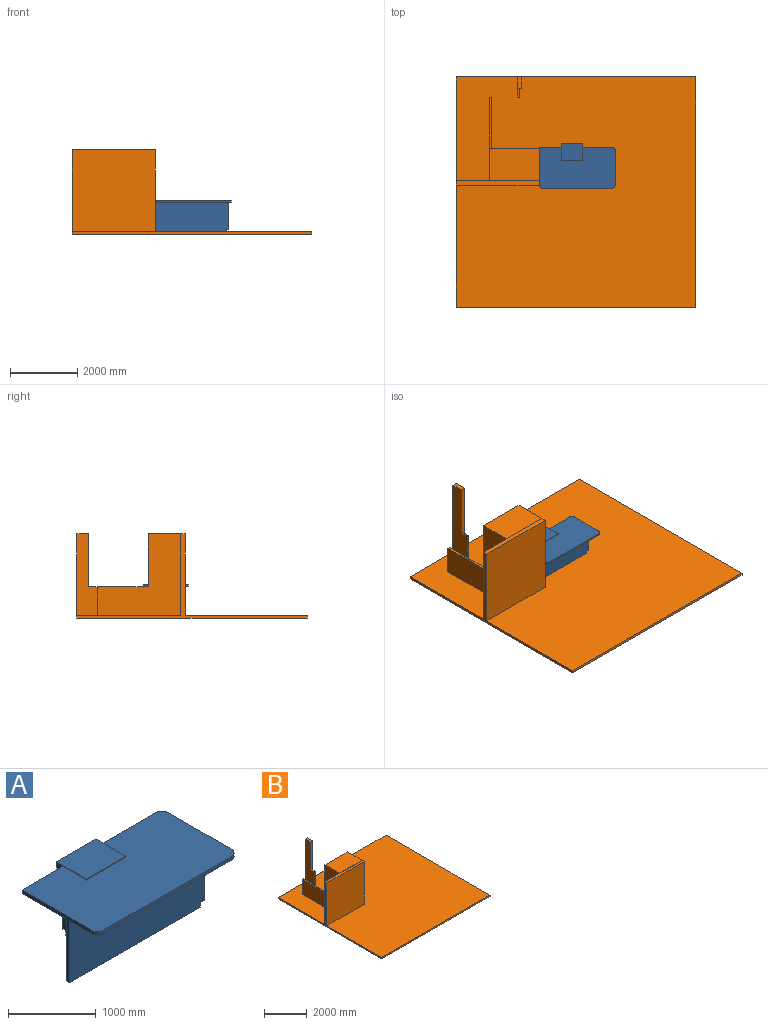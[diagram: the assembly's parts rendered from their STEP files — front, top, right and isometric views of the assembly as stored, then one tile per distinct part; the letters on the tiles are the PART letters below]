
ASSEMBLY  parts=2 mates=2
PART A: 30 faces, bbox 2260.6x1320.8x927.1 mm
  f0: plane 800.1x736.6mm, normal (1,0,0), area 589353.7mm2, adj f3,f5,f7,f28
  f1: plane 1117.6x914.4mm, normal (-1,0,0), area 100645mm2, adj f2,f7,f8,f11,f12,f22,f28,f29
  f2: plane 2114.55x692.15mm, normal (0,0,-1), area 1056328.5mm2, adj f1,f4,f21,f22,f23,f28
  f3: plane 1549.4x736.6mm, normal (0,0,-1), area 117217.5mm2, adj f0,f4,f5,f21,f23,f28
  f4: plane 692.15x63.5mm, normal (1,0,0), area 43951.5mm2, adj f2,f3,f23,f28
  f5: plane 1549.4x800.1mm, normal (0,1,0), area 536289.2mm2, adj f0,f3,f7,f12,f15,f17,f20,f21
  f6: plane 863.6x50.8mm, normal (0,1,0), area 43870.9mm2, adj f7,f11,f14,f17
  f7: plane 2260.6x1219.2mm, normal (0,0,-1), area 1561738.2mm2, adj f0,f1,f5,f6,f9,f10,f13,f14
  f8: plane 660.4x50.8mm, normal (0,1,0), area 33548.3mm2, adj f1,f11,f12,f15
  f9: plane 2057.4x50.8mm, normal (0,-1,0), area 104515.9mm2, adj f7,f11,f13,f29
  f10: plane 1016x50.8mm, normal (1,0,0), area 51612.8mm2, adj f7,f11,f13,f14
  f11: plane 2260.6x1219.2mm, normal (0,0,1), area 2507542.8mm2, adj f1,f6,f8,f9,f10,f13,f14,f15
  f12: plane 711.2x660.4mm, normal (0,0,-1), area 452257.2mm2, adj f1,f5,f8,f15,f21,f22
  f13: cylinder r=101.6mm len=101.6mm, axis (0,0,1), area 8107.3mm2, adj f7,f9,f10,f11
  f14: cylinder r=101.6mm len=101.6mm, axis (0,0,-1), area 8107.3mm2, adj f6,f7,f10,f11
  f15: plane 482.6x171.45mm, normal (-1,0,0), area 25000mm2, adj f5,f8,f11,f12,f16,f18,f19,f20
  f16: plane 635x12.7mm, normal (0,-1,0), area 8064.5mm2, adj f11,f15,f17,f19
  f17: plane 482.6x171.45mm, normal (1,0,0), area 25000mm2, adj f5,f6,f7,f11,f16,f18,f19,f20
  f18: plane 635x171.45mm, normal (0,1,0), area 108870.8mm2, adj f15,f17,f19,f20
  f19: plane 635x482.6mm, normal (0,0,1), area 306451mm2, adj f15,f16,f17,f18
  f20: plane 635x127mm, normal (0,0,-1), area 80645mm2, adj f5,f15,f17,f18
  f21: plane 863.6x685.8mm, normal (-1,0,0), area 589434.3mm2, adj f2,f3,f5,f12,f22,f23
  f22: plane 863.6x635mm, normal (0,1,0), area 548386mm2, adj f1,f2,f12,f21
  f23: plane 1479.55x63.5mm, normal (0,1,0), area 93951.4mm2, adj f2,f3,f4,f21
  f24: plane 781.05x558.8mm, normal (-1,0,0), area 436450.7mm2, adj f5,f7,f25,f27
  f25: plane 812.8x558.8mm, normal (0,0,1), area 454192.6mm2, adj f5,f24,f26,f27
  f26: plane 781.05x558.8mm, normal (1,0,0), area 436450.7mm2, adj f5,f7,f25,f27
  f27: plane 812.8x781.05mm, normal (0,1,0), area 634837.4mm2, adj f7,f24,f25,f26
  f28: plane 2184.4x863.6mm, normal (0,-1,0), area 1882012.4mm2, adj f0,f1,f2,f3,f4,f7
  f29: cylinder r=101.6mm len=101.6mm, axis (0,0,-1), area 8107.3mm2, adj f1,f7,f9,f11
PART B: 25 faces, bbox 7131.1x6858x2514.6 mm
  f0: plane 7131.05x6858mm, normal (0,0,1), area 46957930.3mm2, adj f1,f2,f3,f4,f6,f7,f8,f10
  f1: plane 7131.05x2514.6mm, normal (0,1,0), area 868546.6mm2, adj f0,f2,f4,f5,f18,f19,f21
  f2: plane 6858x2514.6mm, normal (-1,0,0), area 855482.2mm2, adj f0,f1,f3,f5,f6,f7,f9
  f3: plane 7131.05x76.2mm, normal (0,-1,0), area 543386mm2, adj f0,f2,f4,f5
  f4: plane 6858x76.2mm, normal (1,0,0), area 522579.6mm2, adj f0,f1,f3,f5
  f5: plane 7131.05x6858mm, normal (0,0,-1), area 48904740.9mm2, adj f1,f2,f3,f4
  f6: plane 2470.15x2438.4mm, normal (0,1,0), area 6023213.8mm2, adj f0,f2,f8,f9
  f7: plane 2470.15x2438.4mm, normal (0,-1,0), area 6023213.8mm2, adj f0,f2,f8,f9
  f8: plane 2438.4x136.53mm, normal (1,0,0), area 332902.6mm2, adj f0,f6,f7,f9
  f9: plane 2470.15x136.53mm, normal (0,0,1), area 337237.2mm2, adj f2,f6,f7,f8
  f10: plane 2438.4x1492.25mm, normal (0,1,0), area 3578379.9mm2, adj f0,f11,f13,f14,f16,f17
  f11: plane 2476.5x2438.4mm, normal (-1,0,0), area 3658702.4mm2, adj f0,f10,f12,f14,f15,f17
  f12: plane 2438.4x1492.25mm, normal (0,-1,0), area 3638702.4mm2, adj f0,f11,f13,f14
  f13: plane 2438.4x965.2mm, normal (1,0,0), area 2353543.7mm2, adj f0,f10,f12,f14
  f14: plane 1492.25x965.2mm, normal (0,0,1), area 1440319.7mm2, adj f10,f11,f12,f13
  f15: plane 863.6x69.85mm, normal (0,1,0), area 60322.5mm2, adj f0,f11,f16,f17
  f16: plane 1511.3x863.6mm, normal (1,0,0), area 1305158.7mm2, adj f0,f10,f15,f17
  f17: plane 1511.3x69.85mm, normal (0,0,1), area 105564.3mm2, adj f10,f11,f15,f16
  f18: plane 2438.4x342.9mm, normal (1,0,0), area 836127.4mm2, adj f0,f1,f20,f21
  f19: plane 2438.4x600.08mm, normal (-1,0,0), area 1058223.7mm2, adj f0,f1,f20,f21,f22,f24
  f20: plane 2438.4x133.35mm, normal (0,-1,0), area 264838.2mm2, adj f0,f18,f19,f21,f23,f24
  f21: plane 342.9x133.35mm, normal (0,0,1), area 45725.7mm2, adj f1,f18,f19,f20
  f22: plane 863.6x69.85mm, normal (0,-1,0), area 60322.5mm2, adj f0,f19,f23,f24
  f23: plane 863.6x257.18mm, normal (1,0,0), area 222096.3mm2, adj f0,f20,f22,f24
  f24: plane 257.18x69.85mm, normal (0,0,1), area 17963.7mm2, adj f19,f20,f22,f23
PLACE A t=(-188.76,1409.64,-1811.09)mm
PLACE B t=(-2658.91,3532.44,-1811.09)mm fixed
MATE planar B.f10 <-> A.f5  axis (0,1,0) through (-922.89,1409.64,-578.62)mm
MATE planar A.f1 <-> B.f13  axis (-1,0,0) through (-188.76,798.74,-1121.38)mm
